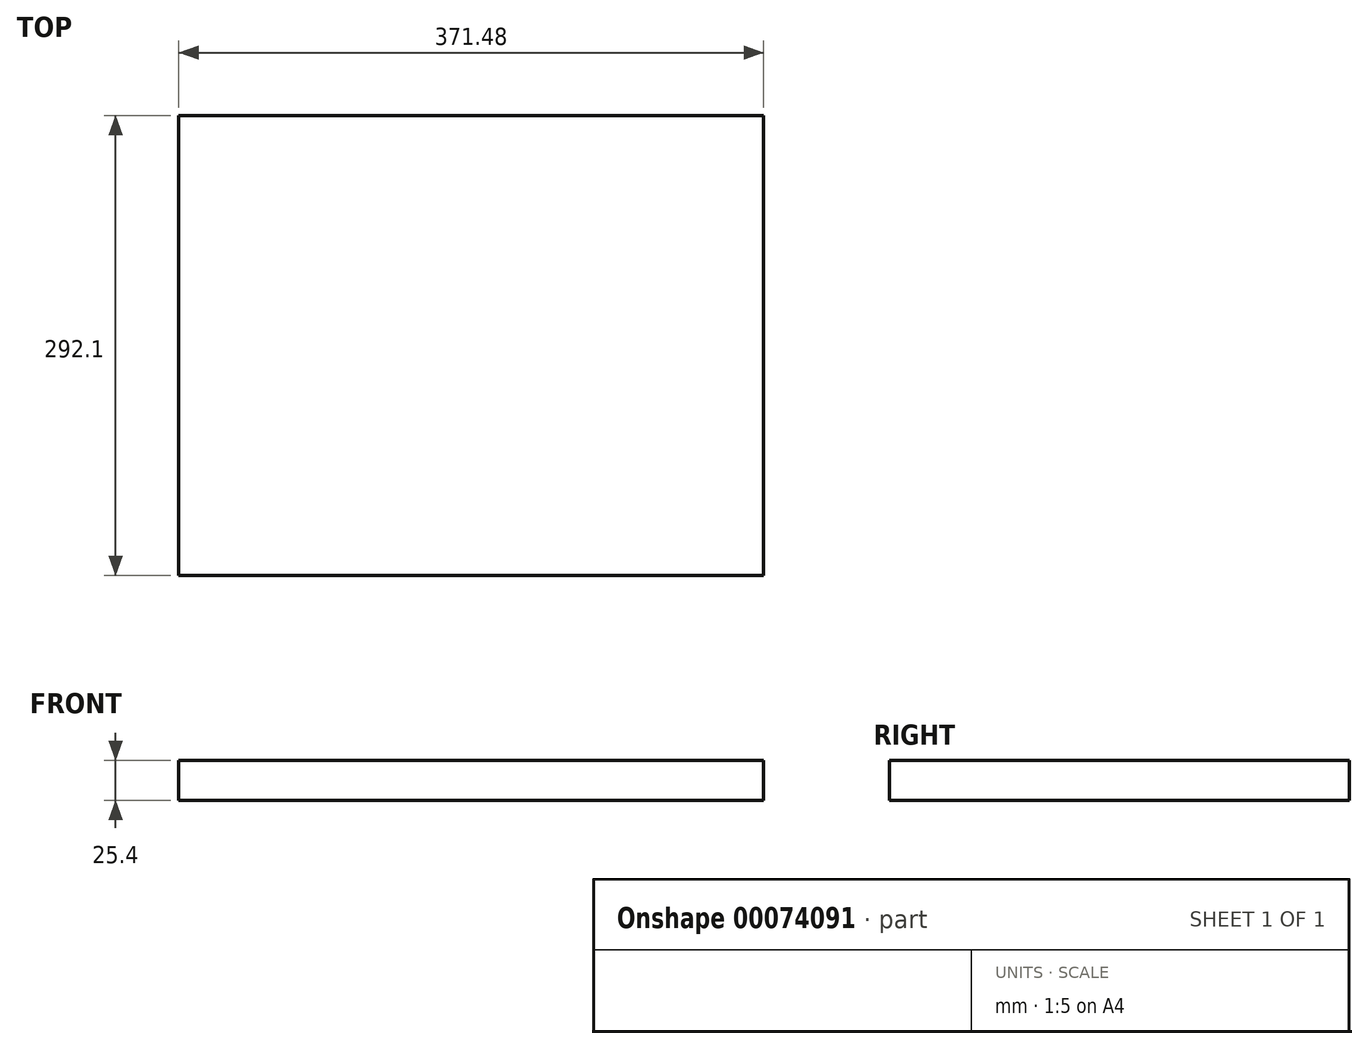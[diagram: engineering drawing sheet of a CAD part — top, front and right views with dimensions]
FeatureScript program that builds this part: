
annotation { "Feature Type Name" : "Feature", "Feature Type Description" : "" }
export const myFeature = defineFeature(function(context is Context, id is Id, definition is map)
    precondition{}
    {
        {
            var Q0;
            Q0=qCreatedBy(makeId("Top.planeOp"),FACE);
            var sketch = newSketch(context, id + "F0", { "sketchPlane" : qUnion([Q0])});
            skLineSegment(sketch, "E0.rect.bottom", {"start": v(185.74, -146.05) * mm, "end": v(-185.74, -146.05) * mm});
            skLineSegment(sketch, "E0.rect.top", {"start": v(185.74, 146.05) * mm, "end": v(-185.74, 146.05) * mm});
            skLineSegment(sketch, "E0.rect.left", {"start": v(185.74, -146.05) * mm, "end": v(185.74, 146.05) * mm});
            skLineSegment(sketch, "E0.rect.right", {"start": v(-185.74, -146.05) * mm, "end": v(-185.74, 146.05) * mm});
            skPoint(sketch, "E0.rect.middle", {"position": v(0, 0) * mm});
            skSolve(sketch);
        }
        {
            var Q0;
            Q0=qSketchRegion(id+"F0",true);
            extrude(context, id + "F1", {"entities" : qUnion([Q0]), "depth" : 25.4 * mm});
        }
    });
